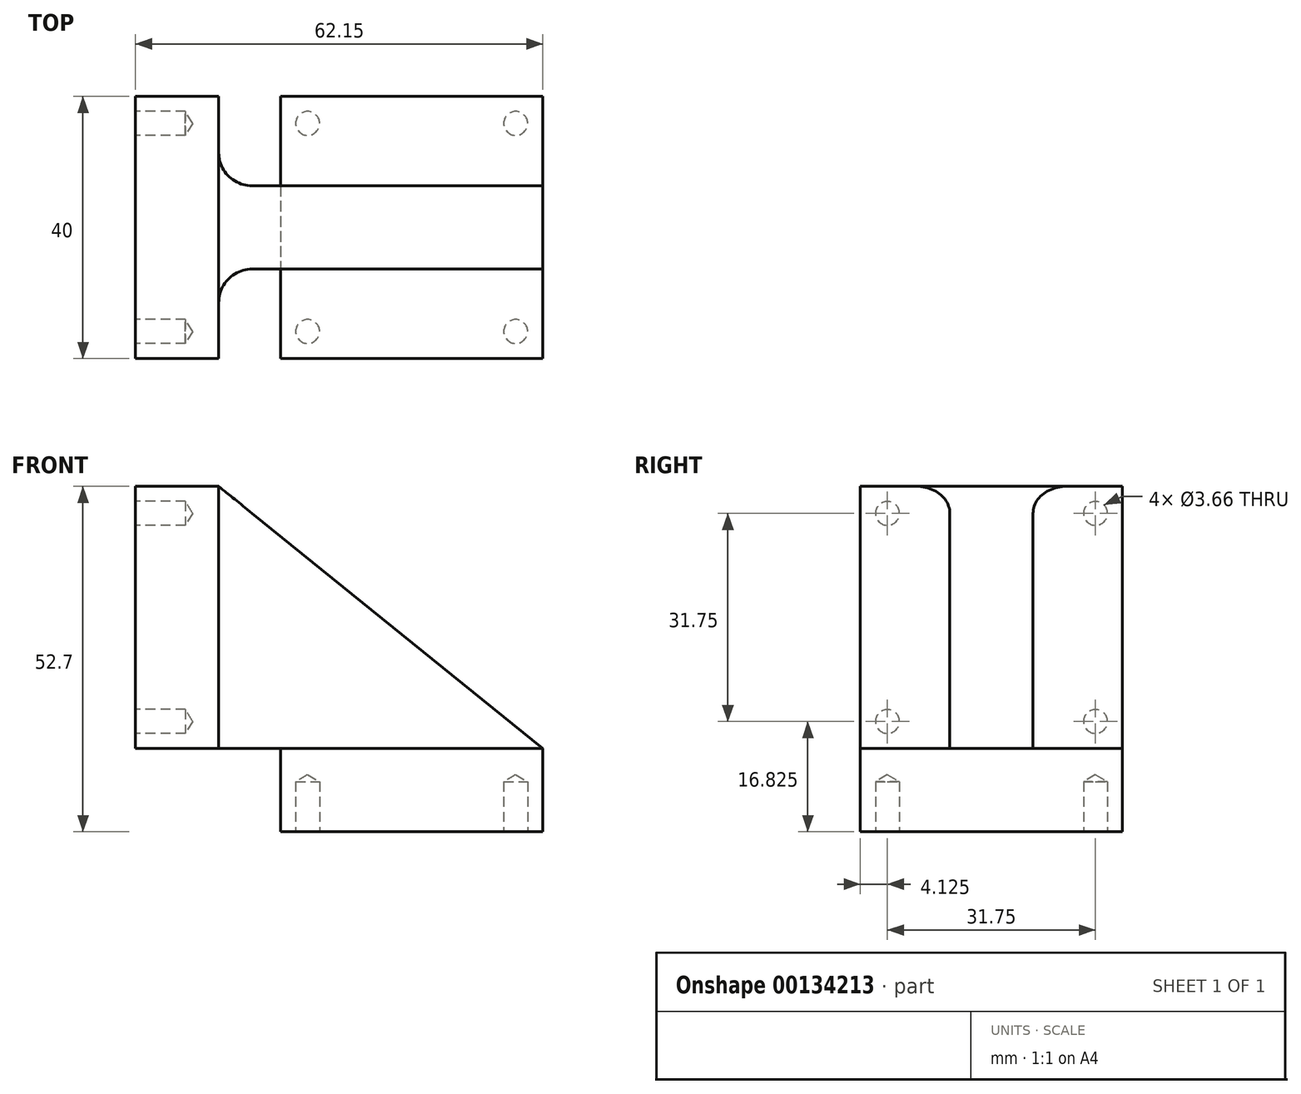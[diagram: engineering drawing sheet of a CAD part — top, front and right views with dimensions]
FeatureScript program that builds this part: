
annotation { "Feature Type Name" : "Feature", "Feature Type Description" : "" }
export const myFeature = defineFeature(function(context is Context, id is Id, definition is map)
    precondition{}
    {
        {
            var Q0;
            Q0=qCreatedBy(makeId("Top.planeOp"),FACE);
            var sketch = newSketch(context, id + "F0", { "sketchPlane" : qUnion([Q0])});
            skLineSegment(sketch, "E0.bottom", {"start": v(20, 20) * mm, "end": v(-20, 20) * mm});
            skLineSegment(sketch, "E0.top", {"start": v(20, -20) * mm, "end": v(-20, -20) * mm});
            skLineSegment(sketch, "E0.left", {"start": v(20, 20) * mm, "end": v(20, -20) * mm});
            skLineSegment(sketch, "E0.right", {"start": v(-20, 20) * mm, "end": v(-20, -20) * mm});
            skPoint(sketch, "E0.middle", {"position": v(0, 0) * mm});
            skPoint(sketch, "E1", {"position": v(15.88, 15.88) * mm});
            skPoint(sketch, "E2.2.0.0", {"position": v(66.67, 15.88) * mm});
            skPoint(sketch, "E3.MirrorP", {"position": v(15.88, -15.88) * mm});
            skPoint(sketch, "E4.MirrorP", {"position": v(-15.88, 15.88) * mm});
            skPoint(sketch, "E5.MirrorP", {"position": v(-15.88, -15.88) * mm});
            skSolve(sketch);
        }
        {
            var Q0;
            Q0 = qSketchRegion(id + "F0", true);
            extrude(context, id + "F1", {"entities" : qUnion([Q0]), "depth" : 12.7 * mm});
        }
        {
            var Q0;
            Q0=makeQuery(id+"F1.opExtrude","CAP_FACE",FACE,{"disambiguationData":[OSD([sQuery(id+"F0.wireOp",EDGE,"E0.bottom"),sQuery(id+"F0.wireOp",EDGE,"E0.top"),sQuery(id+"F0.wireOp",EDGE,"E0.left"),sQuery(id+"F0.wireOp",EDGE,"E0.right")])],"isStart":true});
            var sketch = newSketch(context, id + "F2", { "sketchPlane" : qUnion([Q0])});
            skPoint(sketch, "E6", {"position": v(-15.88, 15.88) * mm});
            skPoint(sketch, "E7.MirrorP", {"position": v(15.88, 15.88) * mm});
            skPoint(sketch, "E8.MirrorP", {"position": v(-15.88, -15.88) * mm});
            skPoint(sketch, "E9.MirrorP", {"position": v(15.88, -15.88) * mm});
            skSolve(sketch);
        }
        {
            var Q0;
            Q0=sQuery(id+"F2.wireOp",VERTEX,"E8.MirrorP");
            var Q1;
            Q1=sQuery(id+"F2.wireOp",VERTEX,"E9.MirrorP");
            var Q2;
            Q2=sQuery(id+"F2.wireOp",VERTEX,"E7.MirrorP");
            var Q3;
            Q3=sQuery(id+"F2.wireOp",VERTEX,"E6");
            var Q4;
            Q4=makeQuery(id+"F1.opExtrude","SWEPT_BODY",BODY,{"disambiguationData":[OSD([sQuery(id+"F0.wireOp",EDGE,"E0.bottom"),sQuery(id+"F0.wireOp",EDGE,"E0.top"),sQuery(id+"F0.wireOp",EDGE,"E0.left"),sQuery(id+"F0.wireOp",EDGE,"E0.right")])]});
            hole(context, id + "F3", {"style" : HoleStyle.SIMPLE, "endStyle" : HoleEndStyle.BLIND, "standardTappedOrClearance" : lookupTablePath({ "standard" : "ANSI", "engagement" : "50%", "pitch" : "32 tpi", "size" : "#8", "type" : "Tapped" }), "standardBlindInLast" : lookupTablePath({ "standard" : "ANSI", "engagement" : "50%", "pitch" : "32 tpi", "size" : "#8", "type" : "Tapped" }), "holeDiameter" : 3.66 * mm, "holeDepth" : 7.62 * mm, "startFromSketch" : true, "locations" : qUnion([Q0, Q1, Q2, Q3]), "scope" : qUnion([Q4]), "majorDiameter" : 4.17 * mm});
        }
        {
            var Q0;
            Q0=makeQuery(id+"F1.opExtrude","CAP_FACE",FACE,{"disambiguationData":[OSD([sQuery(id+"F0.wireOp",EDGE,"E0.bottom"),sQuery(id+"F0.wireOp",EDGE,"E0.top"),sQuery(id+"F0.wireOp",EDGE,"E0.left"),sQuery(id+"F0.wireOp",EDGE,"E0.right")])],"isStart":false});
            var sketch = newSketch(context, id + "F4", { "sketchPlane" : qUnion([Q0])});
            skLineSegment(sketch, "E10.bottom", {"start": v(20, -6.35) * mm, "end": v(-20, -6.35) * mm});
            skLineSegment(sketch, "E10.top", {"start": v(20, 6.35) * mm, "end": v(-20, 6.35) * mm});
            skLineSegment(sketch, "E10.left", {"start": v(20, -6.35) * mm, "end": v(20, 6.35) * mm});
            skLineSegment(sketch, "E10.right", {"start": v(-20, -6.35) * mm, "end": v(-20, 6.35) * mm});
            skPoint(sketch, "E10.middle", {"position": v(0, 0) * mm});
            skSolve(sketch);
        }
        {
            var Q0;
            Q0 = qSketchRegion(id + "F4", true);
            extrude(context, id + "F5", {"entities" : qUnion([Q0]), "operationType" : NewBodyOperationType.ADD, "depth" : 40 * mm});
        }
        {
            var Q0;
            Q0=makeQuery(id+"F5.boolean.opBoolean","MERGE",FACE,{"derivedFrom":[makeQuery(id+"F1.opExtrude","SWEPT_FACE",FACE,{"disambiguationData":[OSD([sQuery(id+"F0.wireOp",EDGE,"E0.right")])]}),makeQuery(id+"F5.opExtrude","SWEPT_FACE",FACE,{"disambiguationData":[OSD([sQuery(id+"F4.wireOp",EDGE,"E10.right")])]})]});
            var sketch = newSketch(context, id + "F6", { "sketchPlane" : qUnion([Q0])});
            skLineSegment(sketch, "E11.bottom", {"start": v(-20, 12.7) * mm, "end": v(20, 12.7) * mm});
            skLineSegment(sketch, "E11.top", {"start": v(-20, 52.7) * mm, "end": v(20, 52.7) * mm});
            skLineSegment(sketch, "E11.left", {"start": v(-20, 12.7) * mm, "end": v(-20, 52.7) * mm});
            skLineSegment(sketch, "E11.right", {"start": v(20, 12.7) * mm, "end": v(20, 52.7) * mm});
            skSolve(sketch);
        }
        {
            var Q0;
            Q0 = qSketchRegion(id + "F6", true);
            extrude(context, id + "F7", {"entities" : qUnion([Q0]), "operationType" : NewBodyOperationType.ADD, "depth" : 22.15 * mm, "hasSecondDirection" : true, "secondDirectionOppositeDirection" : true, "secondDirectionDepth" : 3.05 * mm});
        }
        {
            var Q0;
            Q0=makeQuery(id+"F7.boolean.opBoolean","MERGE",FACE,{"derivedFrom":[makeQuery(id+"F5.opExtrude","CAP_FACE",FACE,{"disambiguationData":[OSD([sQuery(id+"F4.wireOp",EDGE,"E10.bottom"),sQuery(id+"F4.wireOp",EDGE,"E10.top"),sQuery(id+"F4.wireOp",EDGE,"E10.left"),sQuery(id+"F4.wireOp",EDGE,"E10.right")])],"isStart":false}),makeQuery(id+"F7.opExtrude","SWEPT_FACE",FACE,{"disambiguationData":[OSD([sQuery(id+"F6.wireOp",EDGE,"E11.top")])]})]});
            var sketch = newSketch(context, id + "F8", { "sketchPlane" : qUnion([Q0])});
            skLineSegment(sketch, "E12.bottom", {"start": v(-16.95, 20) * mm, "end": v(-29.45, 20) * mm});
            skLineSegment(sketch, "E12.top", {"start": v(-16.95, 6.35) * mm, "end": v(-29.45, 6.35) * mm});
            skLineSegment(sketch, "E12.left", {"start": v(-16.95, 20) * mm, "end": v(-16.95, 6.35) * mm});
            skLineSegment(sketch, "E12.right", {"start": v(-29.45, 20) * mm, "end": v(-29.45, 6.35) * mm});
            skLineSegment(sketch, "E13.bottom", {"start": v(-16.95, -20) * mm, "end": v(-29.45, -20) * mm});
            skLineSegment(sketch, "E13.top", {"start": v(-16.95, -6.35) * mm, "end": v(-29.45, -6.35) * mm});
            skLineSegment(sketch, "E13.left", {"start": v(-16.95, -20) * mm, "end": v(-16.95, -6.35) * mm});
            skLineSegment(sketch, "E13.right", {"start": v(-29.45, -20) * mm, "end": v(-29.45, -6.35) * mm});
            skSolve(sketch);
        }
        {
            var Q0;
            Q0 = qSketchRegion(id + "F8", true);
            extrude(context, id + "F9", {"entities" : qUnion([Q0]), "operationType" : NewBodyOperationType.REMOVE, "oppositeDirection" : true, "depth" : 40 * mm});
        }
        {
            var Q0;
            Q0=makeQuery(id+"F9.boolean.opBoolean","COPY",EDGE,{"derivedFrom":makeQuery(id+"F9.opExtrude","SWEPT_EDGE",EDGE,{"disambiguationData":[OSD([sQuery(id+"F8.wireOp",EDGE,"E13.top"),sQuery(id+"F8.wireOp",EDGE,"E13.right")])]})});
            var Q1;
            Q1=makeQuery(id+"F9.boolean.opBoolean","COPY",EDGE,{"derivedFrom":makeQuery(id+"F9.opExtrude","SWEPT_EDGE",EDGE,{"disambiguationData":[OSD([sQuery(id+"F8.wireOp",EDGE,"E12.top"),sQuery(id+"F8.wireOp",EDGE,"E12.right")])]})});
            fillet(context, id + "F10", {"entities" : qUnion([Q0, Q1]), "radius" : 5.08 * mm, "tangentPropagation" : true, "allowEdgeOverflow" : false});
        }
        {
            var Q0;
            Q0=makeQuery(id+"F7.opExtrude","CAP_FACE",FACE,{"disambiguationData":[OSD([sQuery(id+"F6.wireOp",EDGE,"E11.bottom"),sQuery(id+"F6.wireOp",EDGE,"E11.top"),sQuery(id+"F6.wireOp",EDGE,"E11.left"),sQuery(id+"F6.wireOp",EDGE,"E11.right")])],"isStart":false});
            var sketch = newSketch(context, id + "F11", { "sketchPlane" : qUnion([Q0])});
            skPoint(sketch, "E14", {"position": v(-15.88, 48.57) * mm});
            skPoint(sketch, "E15.MirrorP", {"position": v(15.88, 48.57) * mm});
            skPoint(sketch, "E16", {"position": v(-20, 32.7) * mm});
            skPoint(sketch, "E17", {"position": v(20, 32.7) * mm});
            skLineSegment(sketch, "E18", {"start": v(-20, 32.7) * mm, "end": v(20, 32.7) * mm, "construction": true});
            skPoint(sketch, "E19.MirrorP", {"position": v(-15.88, 16.82) * mm});
            skPoint(sketch, "E20.MirrorP", {"position": v(15.88, 16.82) * mm});
            skSolve(sketch);
        }
        {
            var Q0;
            Q0=sQuery(id+"F11.wireOp",VERTEX,"E14");
            var Q1;
            Q1=sQuery(id+"F11.wireOp",VERTEX,"E15.MirrorP");
            var Q2;
            Q2=sQuery(id+"F11.wireOp",VERTEX,"E20.MirrorP");
            var Q3;
            Q3=sQuery(id+"F11.wireOp",VERTEX,"E19.MirrorP");
            var Q4;
            Q4=makeQuery(id+"F1.opExtrude","SWEPT_BODY",BODY,{"disambiguationData":[OSD([sQuery(id+"F0.wireOp",EDGE,"E0.bottom"),sQuery(id+"F0.wireOp",EDGE,"E0.top"),sQuery(id+"F0.wireOp",EDGE,"E0.left"),sQuery(id+"F0.wireOp",EDGE,"E0.right")])]});
            hole(context, id + "F12", {"style" : HoleStyle.SIMPLE, "endStyle" : HoleEndStyle.BLIND, "standardTappedOrClearance" : lookupTablePath({ "standard" : "ANSI", "engagement" : "50%", "pitch" : "32 tpi", "size" : "#8", "type" : "Tapped" }), "standardBlindInLast" : lookupTablePath({ "standard" : "ANSI", "engagement" : "50%", "pitch" : "32 tpi", "size" : "#8", "type" : "Tapped" }), "holeDiameter" : 3.66 * mm, "holeDepth" : 7.62 * mm, "startFromSketch" : true, "locations" : qUnion([Q0, Q1, Q2, Q3]), "scope" : qUnion([Q4]), "majorDiameter" : 4.17 * mm});
        }
        {
            var Q0;
            Q0=makeQuery(id+"F9.boolean.opBoolean","MERGE",FACE,{"derivedFrom":[makeQuery(id+"F5.opExtrude","SWEPT_FACE",FACE,{"disambiguationData":[OSD([sQuery(id+"F4.wireOp",EDGE,"E10.bottom")])]}),makeQuery(id+"F9.opExtrude","SWEPT_FACE",FACE,{"disambiguationData":[OSD([sQuery(id+"F8.wireOp",EDGE,"E13.top")])]})]});
            var sketch = newSketch(context, id + "F13", { "sketchPlane" : qUnion([Q0])});
            skLineSegment(sketch, "E21", {"start": v(20, 12.7) * mm, "end": v(-29.45, 52.7) * mm});
            skLineSegment(sketch, "E22", {"start": v(-29.45, 52.7) * mm, "end": v(20, 52.7) * mm});
            skLineSegment(sketch, "E23", {"start": v(20, 52.7) * mm, "end": v(20, 12.7) * mm});
            skPoint(sketch, "E24", {"position": v(-24.37, 52.7) * mm});
            skSolve(sketch);
        }
        {
            var Q0;
            {var subQ0=sQuery(id+"F13.wireOp",EDGE,"E22");var subQ1=sQuery(id+"F13.wireOp",EDGE,"E21");var subQ2=makeQuery(id+"F13.imprint","INTERSECT",VERTEX,{"derivedFrom":[subQ1,subQ0]});Q0=makeQuery(id+"F13.imprint","IMPRINT",FACE,{"disambiguationData":[TD([[makeQuery(id+"F13.imprint","IMPRINT",EDGE,{"disambiguationData":[TD([[subQ2,1.0]])],"derivedFrom":subQ1}),-1.0]])]});}
            var Q1;
            {var subQ0=sQuery(id+"F13.wireOp",EDGE,"E23");Q1=makeQuery(id+"F13.imprint","IMPRINT",FACE,{"disambiguationData":[TD([[makeQuery(id+"F13.imprint","IMPRINT",EDGE,{"derivedFrom":subQ0}),-1.0]])]});}
            extrude(context, id + "F14", {"entities" : qUnion([Q0, Q1]), "operationType" : NewBodyOperationType.REMOVE, "endBound" : BoundingType.SYMMETRIC, "oppositeDirection" : true, "depth" : 50.8 * mm});
        }
    });
